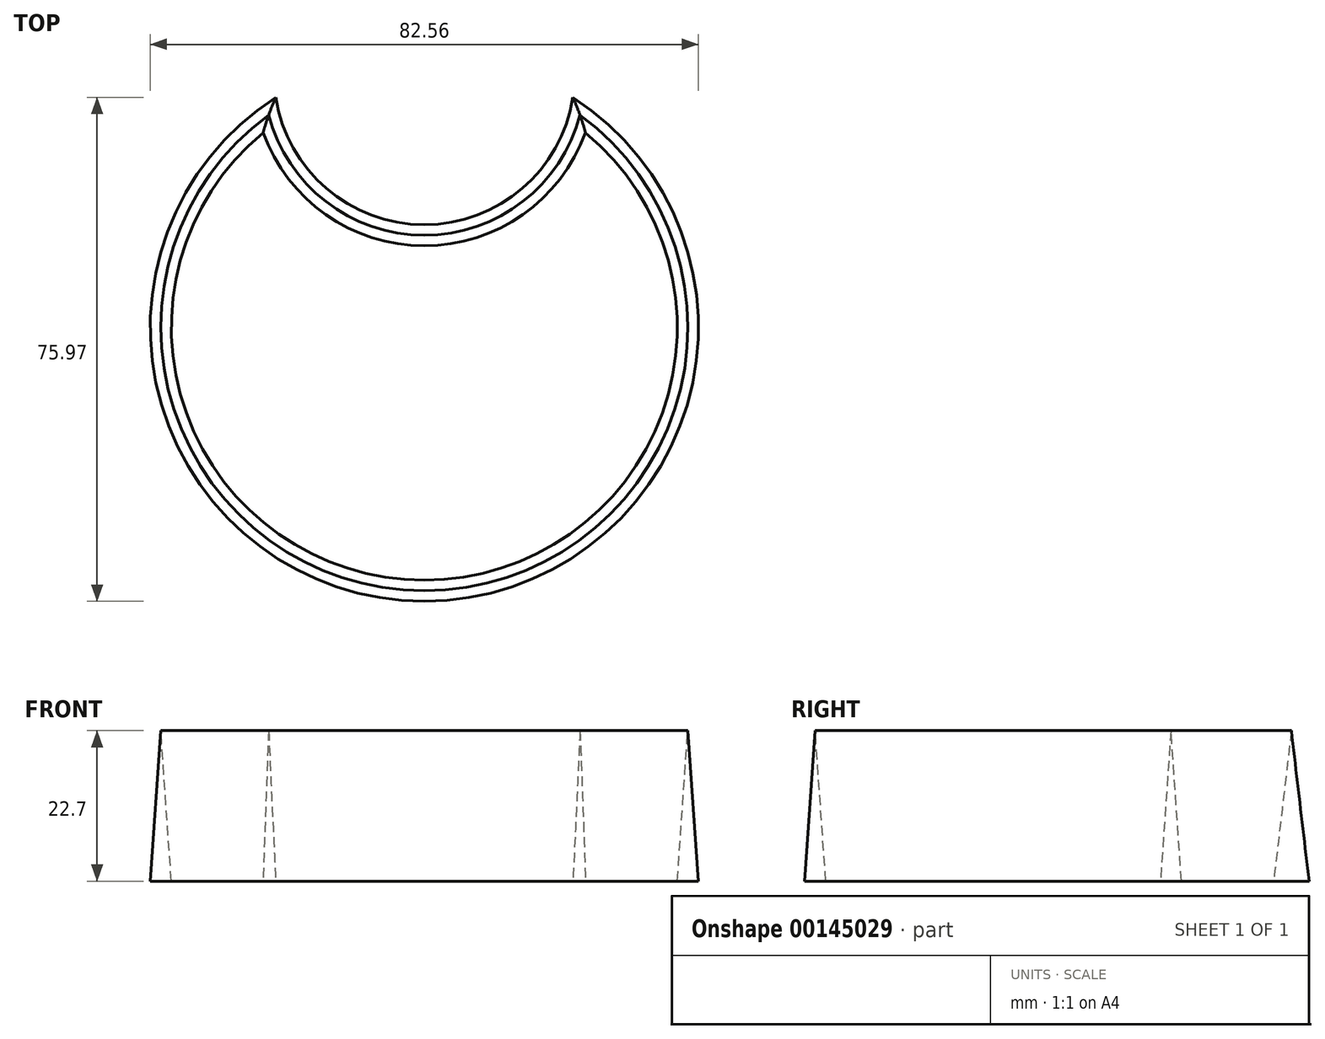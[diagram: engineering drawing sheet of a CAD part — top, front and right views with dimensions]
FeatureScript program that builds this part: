
annotation { "Feature Type Name" : "Feature", "Feature Type Description" : "" }
export const myFeature = defineFeature(function(context is Context, id is Id, definition is map)
    precondition{}
    {
        {
            var Q0;
            Q0=qCreatedBy(makeId("Top.planeOp"),FACE);
            var sketch = newSketch(context, id + "F0", { "sketchPlane" : qUnion([Q0])});
            skArc(sketch, "E0", {"start": v(-24.28, 29.37) * mm, "mid": v(0, -38.1) * mm, "end": v(24.28, 29.37) * mm});
            skLineSegment(sketch, "E1", {"start": v(0, 0) * mm, "end": v(0, 38.1) * mm, "construction": true});
            skArc(sketch, "E2", {"start": v(-24.28, 29.37) * mm, "mid": v(0, 12.3) * mm, "end": v(24.28, 29.37) * mm});
            skPoint(sketch, "E3.orphan", {"position": v(0, 68.55) * mm});
            skArc(sketch, "E4.0", {"start": v(-22.37, 34.69) * mm, "mid": v(0, 15.48) * mm, "end": v(22.37, 34.69) * mm});
            skArc(sketch, "E4.1", {"start": v(-22.37, 34.69) * mm, "mid": v(0, -41.28) * mm, "end": v(22.37, 34.69) * mm});
            skSolve(sketch);
        }
        {
            var Q0;
            Q0=makeQuery(id+"F0.imprint","IMPRINT",FACE,{"disambiguationData":[TD([[makeQuery(id+"F0.imprint","IMPRINT",EDGE,{"derivedFrom":sQuery(id+"F0.wireOp",EDGE,"E0")}),-1.0]])]});
            extrude(context, id + "F1", {"entities" : qUnion([Q0]), "depth" : 25.4 * mm, "hasDraft" : true, "draftAngle" : 4 * degree, "draftPullDirection" : true});
        }
    });
